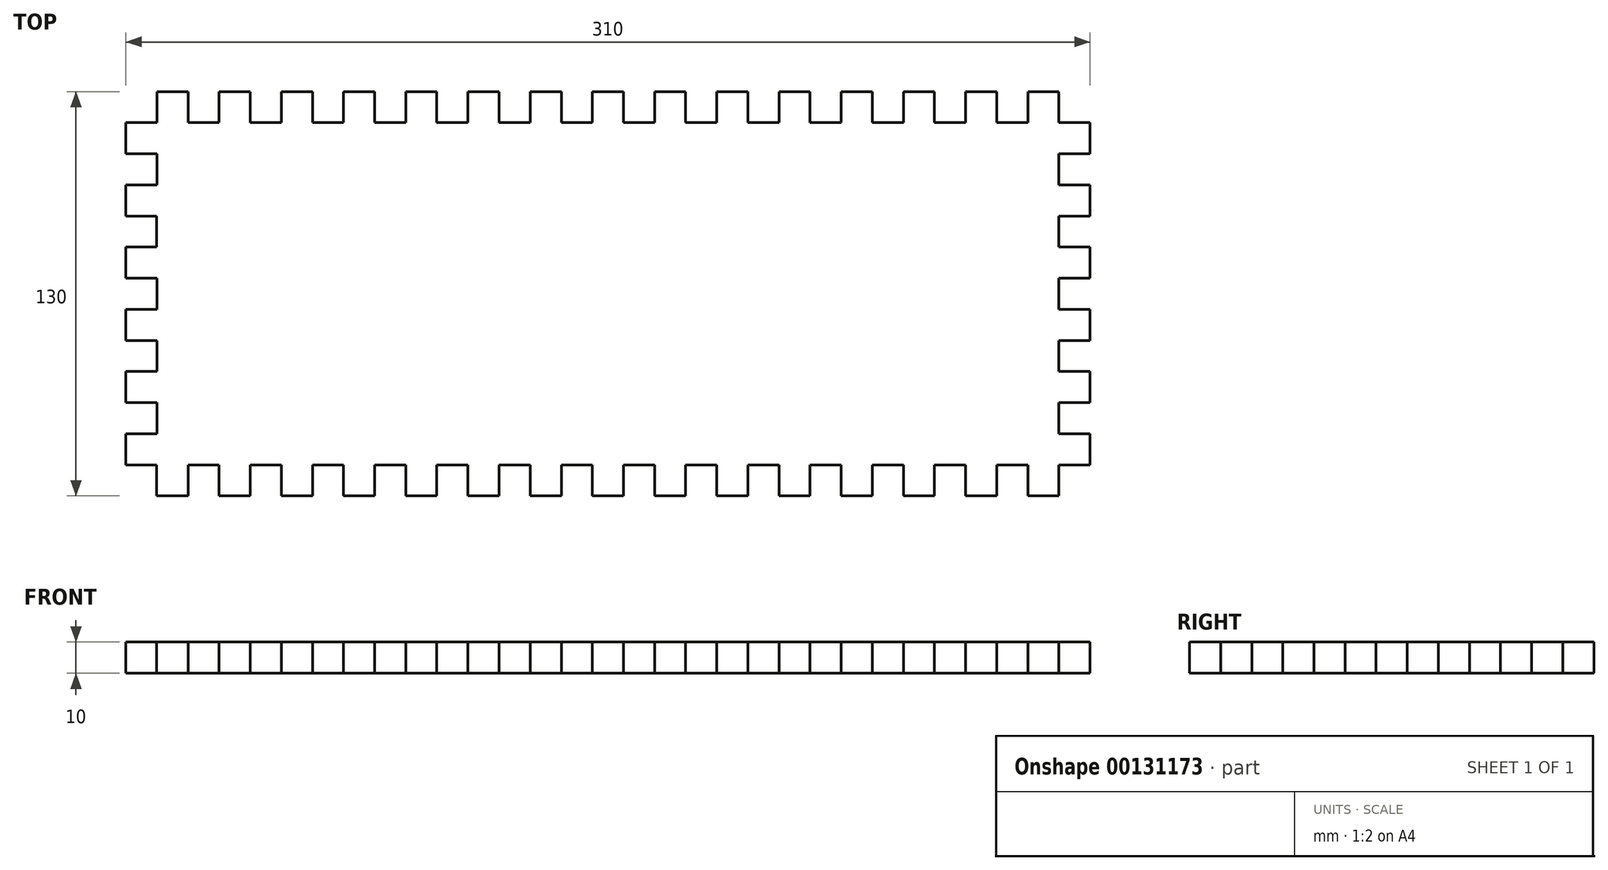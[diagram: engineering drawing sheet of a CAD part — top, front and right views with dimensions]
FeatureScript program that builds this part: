
annotation { "Feature Type Name" : "Feature", "Feature Type Description" : "" }
export const myFeature = defineFeature(function(context is Context, id is Id, definition is map)
    precondition{}
    {
        {
            var Q0;
            Q0=qCreatedBy(makeId("Top.planeOp"),FACE);
            var sketch = newSketch(context, id + "F0", { "sketchPlane" : qUnion([Q0])});
            skLineSegment(sketch, "E0.bottom", {"start": v(-145.09, -65) * mm, "end": v(-135, -65) * mm});
            skLineSegment(sketch, "E0.left", {"start": v(-155, -55) * mm, "end": v(-155, -45) * mm});
            skLineSegment(sketch, "E0.right", {"start": v(155, -55) * mm, "end": v(155, -45) * mm});
            skPoint(sketch, "E0.middle", {"position": v(0, 0) * mm});
            skLineSegment(sketch, "E1.top", {"start": v(-155, 55) * mm, "end": v(-145, 55) * mm});
            skLineSegment(sketch, "E1.right", {"start": v(-145, 65) * mm, "end": v(-145, 55) * mm});
            skLineSegment(sketch, "E2.top", {"start": v(-155, 45) * mm, "end": v(-145, 45) * mm});
            skLineSegment(sketch, "E2.left", {"start": v(-155, 55) * mm, "end": v(-155, 45) * mm});
            skLineSegment(sketch, "E2.right", {"start": v(-145, 55) * mm, "end": v(-145, 45) * mm});
            skLineSegment(sketch, "E3.top", {"start": v(-155, 35) * mm, "end": v(-145, 35) * mm});
            skLineSegment(sketch, "E3.right", {"start": v(-145, 45) * mm, "end": v(-145, 35) * mm});
            skLineSegment(sketch, "E4.top", {"start": v(-155, 25) * mm, "end": v(-145, 25) * mm});
            skLineSegment(sketch, "E4.left", {"start": v(-155, 35) * mm, "end": v(-155, 25) * mm});
            skLineSegment(sketch, "E4.right", {"start": v(-145, 35) * mm, "end": v(-145, 25) * mm});
            skLineSegment(sketch, "E5.bottom", {"start": v(-155, 25) * mm, "end": v(-145.13, 25) * mm});
            skLineSegment(sketch, "E5.top", {"start": v(-155, 15) * mm, "end": v(-145.13, 15) * mm});
            skLineSegment(sketch, "E5.right", {"start": v(-145.13, 25) * mm, "end": v(-145.13, 15) * mm});
            skLineSegment(sketch, "E6.bottom", {"start": v(-155, 15) * mm, "end": v(-145, 15) * mm});
            skLineSegment(sketch, "E6.top", {"start": v(-155, 5) * mm, "end": v(-145, 5) * mm});
            skLineSegment(sketch, "E6.left", {"start": v(-155, 15) * mm, "end": v(-155, 5) * mm});
            skLineSegment(sketch, "E6.right", {"start": v(-145, 15) * mm, "end": v(-145, 5) * mm});
            skPoint(sketch, "E7.orphan", {"position": v(-155, 65) * mm});
            skLineSegment(sketch, "E8.trimOffspring", {"start": v(-155, 45) * mm, "end": v(-155, 55) * mm});
            skLineSegment(sketch, "E9.trimOffspring", {"start": v(-155, 25) * mm, "end": v(-155, 35) * mm});
            skPoint(sketch, "E10.orphan", {"position": v(155, 65) * mm});
            skLineSegment(sketch, "E11.top", {"start": v(-155, -5) * mm, "end": v(-145, -5) * mm});
            skLineSegment(sketch, "E11.right", {"start": v(-145, 5) * mm, "end": v(-145, -5) * mm});
            skLineSegment(sketch, "E12.top", {"start": v(-155, -15) * mm, "end": v(-145, -15) * mm});
            skLineSegment(sketch, "E12.left", {"start": v(-155, -5) * mm, "end": v(-155, -15) * mm});
            skLineSegment(sketch, "E12.right", {"start": v(-145, -5) * mm, "end": v(-145, -15) * mm});
            skLineSegment(sketch, "E13.top", {"start": v(-155, -25) * mm, "end": v(-145, -25) * mm});
            skLineSegment(sketch, "E13.right", {"start": v(-145, -15) * mm, "end": v(-145, -25) * mm});
            skLineSegment(sketch, "E14.top", {"start": v(-155, -35) * mm, "end": v(-145, -35) * mm});
            skLineSegment(sketch, "E14.left", {"start": v(-155, -25) * mm, "end": v(-155, -35) * mm});
            skLineSegment(sketch, "E14.right", {"start": v(-145, -25) * mm, "end": v(-145, -35) * mm});
            skLineSegment(sketch, "E15.top", {"start": v(-155, -45) * mm, "end": v(-145, -45) * mm});
            skLineSegment(sketch, "E15.right", {"start": v(-145, -35) * mm, "end": v(-145, -45) * mm});
            skLineSegment(sketch, "E16.top", {"start": v(-155, -55) * mm, "end": v(-145, -55) * mm});
            skLineSegment(sketch, "E16.left", {"start": v(-155, -45) * mm, "end": v(-155, -55) * mm});
            skLineSegment(sketch, "E16.right", {"start": v(-145, -45) * mm, "end": v(-145, -55) * mm});
            skLineSegment(sketch, "E17.bottom", {"start": v(-155, -55) * mm, "end": v(-145.09, -55) * mm});
            skLineSegment(sketch, "E17.right", {"start": v(-145.09, -55) * mm, "end": v(-145.09, -65) * mm});
            skLineSegment(sketch, "E18.trimOffspring", {"start": v(-155, 5) * mm, "end": v(-155, 15) * mm});
            skLineSegment(sketch, "E19.trimOffspring", {"start": v(-155, -15) * mm, "end": v(-155, -5) * mm});
            skLineSegment(sketch, "E20.trimOffspring", {"start": v(-155, -35) * mm, "end": v(-155, -25) * mm});
            skPoint(sketch, "E21.orphan", {"position": v(-155, -65) * mm});
            skLineSegment(sketch, "E22.bottom", {"start": v(-145, 65) * mm, "end": v(-135, 65) * mm});
            skLineSegment(sketch, "E22.top", {"start": v(-145, 55) * mm, "end": v(-135, 55) * mm});
            skLineSegment(sketch, "E22.right", {"start": v(-135, 65) * mm, "end": v(-135, 55) * mm});
            skLineSegment(sketch, "E23.top", {"start": v(-135, 55) * mm, "end": v(-125, 55) * mm});
            skLineSegment(sketch, "E23.right", {"start": v(-125, 65) * mm, "end": v(-125, 55) * mm});
            skLineSegment(sketch, "E24.bottom", {"start": v(-125, 65) * mm, "end": v(-115, 65) * mm});
            skLineSegment(sketch, "E24.top", {"start": v(-125, 55) * mm, "end": v(-115, 55) * mm});
            skLineSegment(sketch, "E24.right", {"start": v(-115, 65) * mm, "end": v(-115, 55) * mm});
            skLineSegment(sketch, "E25.top", {"start": v(-115, 55) * mm, "end": v(-105, 55) * mm});
            skLineSegment(sketch, "E25.right", {"start": v(-105, 65) * mm, "end": v(-105, 55) * mm});
            skLineSegment(sketch, "E26.bottom", {"start": v(-105, 65) * mm, "end": v(-95, 65) * mm});
            skLineSegment(sketch, "E26.top", {"start": v(-105, 55) * mm, "end": v(-95, 55) * mm});
            skLineSegment(sketch, "E26.right", {"start": v(-95, 65) * mm, "end": v(-95, 55) * mm});
            skLineSegment(sketch, "E27.top", {"start": v(-95, 55) * mm, "end": v(-85, 55) * mm});
            skLineSegment(sketch, "E27.right", {"start": v(-85, 65) * mm, "end": v(-85, 55) * mm});
            skLineSegment(sketch, "E28.bottom", {"start": v(-85, 65) * mm, "end": v(-75, 65) * mm});
            skLineSegment(sketch, "E28.top", {"start": v(-85, 55) * mm, "end": v(-75, 55) * mm});
            skLineSegment(sketch, "E28.right", {"start": v(-75, 65) * mm, "end": v(-75, 55) * mm});
            skLineSegment(sketch, "E29.top", {"start": v(-75, 55) * mm, "end": v(-65, 55) * mm});
            skLineSegment(sketch, "E29.right", {"start": v(-65, 65) * mm, "end": v(-65, 55) * mm});
            skLineSegment(sketch, "E30.bottom", {"start": v(-65, 65) * mm, "end": v(-55, 65) * mm});
            skLineSegment(sketch, "E30.top", {"start": v(-65, 55) * mm, "end": v(-55, 55) * mm});
            skLineSegment(sketch, "E30.right", {"start": v(-55, 65) * mm, "end": v(-55, 55) * mm});
            skLineSegment(sketch, "E31.top", {"start": v(-55, 55) * mm, "end": v(-45, 55) * mm});
            skLineSegment(sketch, "E31.right", {"start": v(-45, 65) * mm, "end": v(-45, 55) * mm});
            skLineSegment(sketch, "E32.bottom", {"start": v(-45, 65) * mm, "end": v(-35, 65) * mm});
            skLineSegment(sketch, "E32.top", {"start": v(-45, 55) * mm, "end": v(-35, 55) * mm});
            skLineSegment(sketch, "E32.right", {"start": v(-35, 65) * mm, "end": v(-35, 55) * mm});
            skLineSegment(sketch, "E33.top", {"start": v(-35, 55) * mm, "end": v(-25, 55) * mm});
            skLineSegment(sketch, "E33.right", {"start": v(-25, 65) * mm, "end": v(-25, 55) * mm});
            skLineSegment(sketch, "E34.bottom", {"start": v(-25, 65) * mm, "end": v(-15, 65) * mm});
            skLineSegment(sketch, "E34.top", {"start": v(-25, 55) * mm, "end": v(-15, 55) * mm});
            skLineSegment(sketch, "E34.right", {"start": v(-15, 65) * mm, "end": v(-15, 55) * mm});
            skLineSegment(sketch, "E35.top", {"start": v(-15, 55) * mm, "end": v(-5, 55) * mm});
            skLineSegment(sketch, "E35.right", {"start": v(-5, 65) * mm, "end": v(-5, 55) * mm});
            skLineSegment(sketch, "E36.bottom", {"start": v(-5, 65) * mm, "end": v(5, 65) * mm});
            skLineSegment(sketch, "E36.top", {"start": v(-5, 54.5) * mm, "end": v(5, 54.5) * mm});
            skLineSegment(sketch, "E36.left", {"start": v(-5, 65) * mm, "end": v(-5, 54.5) * mm});
            skLineSegment(sketch, "E36.right", {"start": v(5, 65) * mm, "end": v(5, 54.5) * mm});
            skLineSegment(sketch, "E37.top", {"start": v(5, 55) * mm, "end": v(15, 55) * mm});
            skLineSegment(sketch, "E37.left", {"start": v(5, 65) * mm, "end": v(5, 55) * mm});
            skLineSegment(sketch, "E37.right", {"start": v(15, 65) * mm, "end": v(15, 55) * mm});
            skLineSegment(sketch, "E38.bottom", {"start": v(15, 65) * mm, "end": v(25, 65) * mm});
            skLineSegment(sketch, "E38.top", {"start": v(15, 55) * mm, "end": v(25, 55) * mm});
            skLineSegment(sketch, "E38.right", {"start": v(25, 65) * mm, "end": v(25, 55) * mm});
            skLineSegment(sketch, "E39.top", {"start": v(25, 55) * mm, "end": v(35, 55) * mm});
            skLineSegment(sketch, "E39.right", {"start": v(35, 65) * mm, "end": v(35, 55) * mm});
            skLineSegment(sketch, "E40.bottom", {"start": v(35, 65) * mm, "end": v(45, 65) * mm});
            skLineSegment(sketch, "E40.top", {"start": v(35, 55) * mm, "end": v(45, 55) * mm});
            skLineSegment(sketch, "E40.right", {"start": v(45, 65) * mm, "end": v(45, 55) * mm});
            skLineSegment(sketch, "E41.top", {"start": v(45, 55) * mm, "end": v(55, 55) * mm});
            skLineSegment(sketch, "E41.right", {"start": v(55, 65) * mm, "end": v(55, 55) * mm});
            skLineSegment(sketch, "E42.bottom", {"start": v(55, 65) * mm, "end": v(65, 65) * mm});
            skLineSegment(sketch, "E42.top", {"start": v(55, 55) * mm, "end": v(65, 55) * mm});
            skLineSegment(sketch, "E42.right", {"start": v(65, 65) * mm, "end": v(65, 55) * mm});
            skLineSegment(sketch, "E43.top", {"start": v(65, 55) * mm, "end": v(75, 55) * mm});
            skLineSegment(sketch, "E43.right", {"start": v(75, 65) * mm, "end": v(75, 55) * mm});
            skLineSegment(sketch, "E44.bottom", {"start": v(75, 65) * mm, "end": v(85, 65) * mm});
            skLineSegment(sketch, "E44.top", {"start": v(75, 55) * mm, "end": v(85, 55) * mm});
            skLineSegment(sketch, "E44.right", {"start": v(85, 65) * mm, "end": v(85, 55) * mm});
            skLineSegment(sketch, "E45.top", {"start": v(85, 55) * mm, "end": v(95, 55) * mm});
            skLineSegment(sketch, "E45.right", {"start": v(95, 65) * mm, "end": v(95, 55) * mm});
            skLineSegment(sketch, "E46.bottom", {"start": v(95, 65) * mm, "end": v(105, 65) * mm});
            skLineSegment(sketch, "E46.top", {"start": v(95, 55) * mm, "end": v(105, 55) * mm});
            skLineSegment(sketch, "E46.right", {"start": v(105, 65) * mm, "end": v(105, 55) * mm});
            skLineSegment(sketch, "E47.top", {"start": v(105, 55) * mm, "end": v(115, 55) * mm});
            skLineSegment(sketch, "E47.right", {"start": v(115, 65) * mm, "end": v(115, 55) * mm});
            skLineSegment(sketch, "E48.bottom", {"start": v(115, 65) * mm, "end": v(125, 65) * mm});
            skLineSegment(sketch, "E48.top", {"start": v(115, 55) * mm, "end": v(125, 55) * mm});
            skLineSegment(sketch, "E48.right", {"start": v(125, 65) * mm, "end": v(125, 55) * mm});
            skLineSegment(sketch, "E49.top", {"start": v(125, 55) * mm, "end": v(135, 55) * mm});
            skLineSegment(sketch, "E49.right", {"start": v(135, 65) * mm, "end": v(135, 55) * mm});
            skLineSegment(sketch, "E50.bottom", {"start": v(135, 65) * mm, "end": v(145, 65) * mm});
            skLineSegment(sketch, "E50.top", {"start": v(135, 55) * mm, "end": v(145, 55) * mm});
            skLineSegment(sketch, "E50.right", {"start": v(145, 65) * mm, "end": v(145, 55) * mm});
            skLineSegment(sketch, "E51.top", {"start": v(145, 55) * mm, "end": v(155, 55) * mm});
            skLineSegment(sketch, "E52.bottom", {"start": v(-145, -55) * mm, "end": v(-135, -55) * mm});
            skLineSegment(sketch, "E52.top", {"start": v(-145, -65) * mm, "end": v(-135, -65) * mm});
            skLineSegment(sketch, "E52.left", {"start": v(-145, -55) * mm, "end": v(-145, -65) * mm});
            skLineSegment(sketch, "E52.right", {"start": v(-135, -55) * mm, "end": v(-135, -65) * mm});
            skLineSegment(sketch, "E53.bottom", {"start": v(-135, -55) * mm, "end": v(-125, -55) * mm});
            skLineSegment(sketch, "E53.right", {"start": v(-125, -55) * mm, "end": v(-125, -65) * mm});
            skLineSegment(sketch, "E54.bottom", {"start": v(-125, -55) * mm, "end": v(-115, -55) * mm});
            skLineSegment(sketch, "E54.top", {"start": v(-125, -65) * mm, "end": v(-115, -65) * mm});
            skLineSegment(sketch, "E54.right", {"start": v(-115, -55) * mm, "end": v(-115, -65) * mm});
            skLineSegment(sketch, "E55.bottom", {"start": v(-115, -55) * mm, "end": v(-105, -55) * mm});
            skLineSegment(sketch, "E55.right", {"start": v(-105, -55) * mm, "end": v(-105, -65) * mm});
            skLineSegment(sketch, "E56.bottom", {"start": v(-105, -55) * mm, "end": v(-95, -55) * mm});
            skLineSegment(sketch, "E56.top", {"start": v(-105, -65) * mm, "end": v(-95, -65) * mm});
            skLineSegment(sketch, "E56.right", {"start": v(-95, -55) * mm, "end": v(-95, -65) * mm});
            skLineSegment(sketch, "E57.bottom", {"start": v(-95, -55) * mm, "end": v(-85, -55) * mm});
            skLineSegment(sketch, "E57.right", {"start": v(-85, -55) * mm, "end": v(-85, -65) * mm});
            skLineSegment(sketch, "E58.bottom", {"start": v(-85, -55) * mm, "end": v(-75, -55) * mm});
            skLineSegment(sketch, "E58.top", {"start": v(-85, -65) * mm, "end": v(-75, -65) * mm});
            skLineSegment(sketch, "E58.right", {"start": v(-75, -55) * mm, "end": v(-75, -65) * mm});
            skLineSegment(sketch, "E59.bottom", {"start": v(-75, -55) * mm, "end": v(-65, -55) * mm});
            skLineSegment(sketch, "E59.right", {"start": v(-65, -55) * mm, "end": v(-65, -65) * mm});
            skLineSegment(sketch, "E60.bottom", {"start": v(-65, -55) * mm, "end": v(-55, -55) * mm});
            skLineSegment(sketch, "E60.top", {"start": v(-65, -65) * mm, "end": v(-55, -65) * mm});
            skLineSegment(sketch, "E60.right", {"start": v(-55, -55) * mm, "end": v(-55, -65) * mm});
            skLineSegment(sketch, "E61.bottom", {"start": v(-55, -55) * mm, "end": v(-45, -55) * mm});
            skLineSegment(sketch, "E61.right", {"start": v(-45, -55) * mm, "end": v(-45, -65) * mm});
            skLineSegment(sketch, "E62.bottom", {"start": v(-45, -55) * mm, "end": v(-35, -55) * mm});
            skLineSegment(sketch, "E62.top", {"start": v(-45, -65) * mm, "end": v(-35, -65) * mm});
            skLineSegment(sketch, "E62.right", {"start": v(-35, -55) * mm, "end": v(-35, -65) * mm});
            skLineSegment(sketch, "E63.bottom", {"start": v(-35, -55) * mm, "end": v(-25, -55) * mm});
            skLineSegment(sketch, "E63.right", {"start": v(-25, -55) * mm, "end": v(-25, -65) * mm});
            skLineSegment(sketch, "E64.bottom", {"start": v(-25, -55) * mm, "end": v(-15, -55) * mm});
            skLineSegment(sketch, "E64.top", {"start": v(-25, -65) * mm, "end": v(-15, -65) * mm});
            skLineSegment(sketch, "E64.right", {"start": v(-15, -55) * mm, "end": v(-15, -65) * mm});
            skLineSegment(sketch, "E65.bottom", {"start": v(-15, -55) * mm, "end": v(-5, -55) * mm});
            skLineSegment(sketch, "E65.right", {"start": v(-5, -55) * mm, "end": v(-5, -65) * mm});
            skLineSegment(sketch, "E66.bottom", {"start": v(-5, -55) * mm, "end": v(5, -55) * mm});
            skLineSegment(sketch, "E66.top", {"start": v(-5, -65) * mm, "end": v(5, -65) * mm});
            skLineSegment(sketch, "E66.right", {"start": v(5, -55) * mm, "end": v(5, -65) * mm});
            skLineSegment(sketch, "E67.bottom", {"start": v(5, -55) * mm, "end": v(15, -55) * mm});
            skLineSegment(sketch, "E67.right", {"start": v(15, -55) * mm, "end": v(15, -65) * mm});
            skLineSegment(sketch, "E68.bottom", {"start": v(15, -55) * mm, "end": v(25, -55) * mm});
            skLineSegment(sketch, "E68.top", {"start": v(15, -65) * mm, "end": v(25, -65) * mm});
            skLineSegment(sketch, "E68.right", {"start": v(25, -55) * mm, "end": v(25, -65) * mm});
            skLineSegment(sketch, "E69.bottom", {"start": v(25, -55) * mm, "end": v(35, -55) * mm});
            skLineSegment(sketch, "E69.right", {"start": v(35, -55) * mm, "end": v(35, -65) * mm});
            skLineSegment(sketch, "E70.bottom", {"start": v(35, -55) * mm, "end": v(45, -55) * mm});
            skLineSegment(sketch, "E70.top", {"start": v(35, -65) * mm, "end": v(45, -65) * mm});
            skLineSegment(sketch, "E70.right", {"start": v(45, -55) * mm, "end": v(45, -65) * mm});
            skLineSegment(sketch, "E71.bottom", {"start": v(45, -55) * mm, "end": v(55, -55) * mm});
            skLineSegment(sketch, "E71.right", {"start": v(55, -55) * mm, "end": v(55, -65) * mm});
            skLineSegment(sketch, "E72.bottom", {"start": v(55, -55) * mm, "end": v(65, -55) * mm});
            skLineSegment(sketch, "E72.top", {"start": v(55, -65) * mm, "end": v(65, -65) * mm});
            skLineSegment(sketch, "E72.right", {"start": v(65, -55) * mm, "end": v(65, -65) * mm});
            skLineSegment(sketch, "E73.bottom", {"start": v(65, -55) * mm, "end": v(75, -55) * mm});
            skLineSegment(sketch, "E73.right", {"start": v(75, -55) * mm, "end": v(75, -65) * mm});
            skLineSegment(sketch, "E74.bottom", {"start": v(75, -55) * mm, "end": v(85, -55) * mm});
            skLineSegment(sketch, "E74.top", {"start": v(75, -65) * mm, "end": v(85, -65) * mm});
            skLineSegment(sketch, "E74.right", {"start": v(85, -55) * mm, "end": v(85, -65) * mm});
            skLineSegment(sketch, "E75.bottom", {"start": v(85, -55) * mm, "end": v(95, -55) * mm});
            skLineSegment(sketch, "E75.right", {"start": v(95, -55) * mm, "end": v(95, -65) * mm});
            skLineSegment(sketch, "E76.bottom", {"start": v(95, -55) * mm, "end": v(105, -55) * mm});
            skLineSegment(sketch, "E76.top", {"start": v(95, -65) * mm, "end": v(105, -65) * mm});
            skLineSegment(sketch, "E76.right", {"start": v(105, -55) * mm, "end": v(105, -65) * mm});
            skLineSegment(sketch, "E77.bottom", {"start": v(105, -55) * mm, "end": v(115, -55) * mm});
            skLineSegment(sketch, "E77.right", {"start": v(115, -55) * mm, "end": v(115, -65) * mm});
            skLineSegment(sketch, "E78.bottom", {"start": v(115, -55) * mm, "end": v(125, -55) * mm});
            skLineSegment(sketch, "E78.top", {"start": v(115, -65) * mm, "end": v(125, -65) * mm});
            skLineSegment(sketch, "E78.right", {"start": v(125, -55) * mm, "end": v(125, -65) * mm});
            skLineSegment(sketch, "E79.bottom", {"start": v(125, -55) * mm, "end": v(135, -55) * mm});
            skLineSegment(sketch, "E79.right", {"start": v(135, -55) * mm, "end": v(135, -65) * mm});
            skLineSegment(sketch, "E80.bottom", {"start": v(135, -55) * mm, "end": v(145, -55) * mm});
            skLineSegment(sketch, "E80.top", {"start": v(135, -65) * mm, "end": v(145, -65) * mm});
            skLineSegment(sketch, "E80.right", {"start": v(145, -55) * mm, "end": v(145, -65) * mm});
            skLineSegment(sketch, "E81.bottom", {"start": v(145, -55) * mm, "end": v(155, -55) * mm});
            skPoint(sketch, "E81.right.end.orphan", {"position": v(155, -65) * mm});
            skLineSegment(sketch, "E82.top", {"start": v(145, 45) * mm, "end": v(155, 45) * mm});
            skLineSegment(sketch, "E82.left", {"start": v(145, 55) * mm, "end": v(145, 45) * mm});
            skLineSegment(sketch, "E82.right", {"start": v(155, 55) * mm, "end": v(155, 45) * mm});
            skLineSegment(sketch, "E83.top", {"start": v(145, 35) * mm, "end": v(155, 35) * mm});
            skLineSegment(sketch, "E83.left", {"start": v(145, 45) * mm, "end": v(145, 35) * mm});
            skLineSegment(sketch, "E84.top", {"start": v(145, 25) * mm, "end": v(155, 25) * mm});
            skLineSegment(sketch, "E84.left", {"start": v(145, 35) * mm, "end": v(145, 25) * mm});
            skLineSegment(sketch, "E84.right", {"start": v(155, 35) * mm, "end": v(155, 25) * mm});
            skLineSegment(sketch, "E85.top", {"start": v(145, 15) * mm, "end": v(155, 15) * mm});
            skLineSegment(sketch, "E85.left", {"start": v(145, 25) * mm, "end": v(145, 15) * mm});
            skLineSegment(sketch, "E86.top", {"start": v(145, 5) * mm, "end": v(155, 5) * mm});
            skLineSegment(sketch, "E86.left", {"start": v(145, 15) * mm, "end": v(145, 5) * mm});
            skLineSegment(sketch, "E86.right", {"start": v(155, 15) * mm, "end": v(155, 5) * mm});
            skLineSegment(sketch, "E87.top", {"start": v(145, -5) * mm, "end": v(155, -5) * mm});
            skLineSegment(sketch, "E87.left", {"start": v(145, 5) * mm, "end": v(145, -5) * mm});
            skLineSegment(sketch, "E88.top", {"start": v(145, -15) * mm, "end": v(155, -15) * mm});
            skLineSegment(sketch, "E88.left", {"start": v(145, -5) * mm, "end": v(145, -15) * mm});
            skLineSegment(sketch, "E88.right", {"start": v(155, -5) * mm, "end": v(155, -15) * mm});
            skLineSegment(sketch, "E89.top", {"start": v(145, -25) * mm, "end": v(155, -25) * mm});
            skLineSegment(sketch, "E89.left", {"start": v(145, -15) * mm, "end": v(145, -25) * mm});
            skLineSegment(sketch, "E90.top", {"start": v(145, -35) * mm, "end": v(155, -35) * mm});
            skLineSegment(sketch, "E90.left", {"start": v(145, -25) * mm, "end": v(145, -35) * mm});
            skLineSegment(sketch, "E90.right", {"start": v(155, -25) * mm, "end": v(155, -35) * mm});
            skLineSegment(sketch, "E91.top", {"start": v(145, -45) * mm, "end": v(155, -45) * mm});
            skLineSegment(sketch, "E91.left", {"start": v(145, -35) * mm, "end": v(145, -45) * mm});
            skLineSegment(sketch, "E92", {"start": v(145, -45) * mm, "end": v(145, -55) * mm});
            skLineSegment(sketch, "E93.trimOffspring", {"start": v(155, 45) * mm, "end": v(155, 55) * mm});
            skLineSegment(sketch, "E94.trimOffspring", {"start": v(155, 25) * mm, "end": v(155, 35) * mm});
            skLineSegment(sketch, "E95.trimOffspring", {"start": v(155, 5) * mm, "end": v(155, 15) * mm});
            skLineSegment(sketch, "E96.trimOffspring", {"start": v(155, -15) * mm, "end": v(155, -5) * mm});
            skLineSegment(sketch, "E97.trimOffspring", {"start": v(155, -35) * mm, "end": v(155, -25) * mm});
            skSolve(sketch);
        }
        {
            var Q0;
            Q0=makeQuery(id+"F0.imprint","IMPRINT",FACE,{"disambiguationData":[TD([[makeQuery(id+"F0.imprint","IMPRINT",EDGE,{"derivedFrom":sQuery(id+"F0.wireOp",EDGE,"E0.bottom")}),1.0]])]});
            var Q1;
            Q1=makeQuery(id+"F0.imprint","IMPRINT",FACE,{"disambiguationData":[TD([[makeQuery(id+"F0.imprint","IMPRINT",EDGE,{"derivedFrom":sQuery(id+"F0.wireOp",EDGE,"E1.top")}),-1.0]])]});
            var Q2;
            Q2=makeQuery(id+"F0.imprint","IMPRINT",FACE,{"disambiguationData":[TD([[makeQuery(id+"F0.imprint","IMPRINT",EDGE,{"derivedFrom":sQuery(id+"F0.wireOp",EDGE,"E3.top")}),-1.0]])]});
            var Q3;
            {var subQ2=sQuery(id+"F0.wireOp",EDGE,"E6.right");Q3=makeQuery(id+"F0.imprint","IMPRINT",FACE,{"disambiguationData":[TD([[makeQuery(id+"F0.imprint","IMPRINT",EDGE,{"derivedFrom":subQ2}),-1.0]])]});}
            var Q4;
            Q4=makeQuery(id+"F0.imprint","IMPRINT",FACE,{"disambiguationData":[TD([[makeQuery(id+"F0.imprint","IMPRINT",EDGE,{"derivedFrom":sQuery(id+"F0.wireOp",EDGE,"E11.top")}),-1.0]])]});
            var Q5;
            Q5=makeQuery(id+"F0.imprint","IMPRINT",FACE,{"disambiguationData":[TD([[makeQuery(id+"F0.imprint","IMPRINT",EDGE,{"derivedFrom":sQuery(id+"F0.wireOp",EDGE,"E13.top")}),-1.0]])]});
            var Q6;
            Q6=makeQuery(id+"F0.imprint","IMPRINT",FACE,{"disambiguationData":[TD([[makeQuery(id+"F0.imprint","IMPRINT",EDGE,{"derivedFrom":sQuery(id+"F0.wireOp",EDGE,"E15.top")}),-1.0]])]});
            var Q7;
            Q7=makeQuery(id+"F0.imprint","IMPRINT",FACE,{"disambiguationData":[TD([[makeQuery(id+"F0.imprint","IMPRINT",EDGE,{"derivedFrom":sQuery(id+"F0.wireOp",EDGE,"E52.bottom")}),-1.0]])]});
            var Q8;
            Q8=makeQuery(id+"F0.imprint","IMPRINT",FACE,{"disambiguationData":[TD([[makeQuery(id+"F0.imprint","IMPRINT",EDGE,{"derivedFrom":sQuery(id+"F0.wireOp",EDGE,"E0.right")}),1.0]])]});
            var Q9;
            Q9=makeQuery(id+"F0.imprint","IMPRINT",FACE,{"disambiguationData":[TD([[makeQuery(id+"F0.imprint","IMPRINT",EDGE,{"derivedFrom":sQuery(id+"F0.wireOp",EDGE,"E22.bottom")}),-1.0]])]});
            var Q10;
            Q10=makeQuery(id+"F0.imprint","IMPRINT",FACE,{"disambiguationData":[TD([[makeQuery(id+"F0.imprint","IMPRINT",EDGE,{"derivedFrom":sQuery(id+"F0.wireOp",EDGE,"E24.top")}),1.0]])]});
            var Q11;
            Q11=makeQuery(id+"F0.imprint","IMPRINT",FACE,{"disambiguationData":[TD([[makeQuery(id+"F0.imprint","IMPRINT",EDGE,{"derivedFrom":sQuery(id+"F0.wireOp",EDGE,"E26.bottom")}),-1.0]])]});
            var Q12;
            Q12=makeQuery(id+"F0.imprint","IMPRINT",FACE,{"disambiguationData":[TD([[makeQuery(id+"F0.imprint","IMPRINT",EDGE,{"derivedFrom":sQuery(id+"F0.wireOp",EDGE,"E28.top")}),1.0]])]});
            var Q13;
            Q13=makeQuery(id+"F0.imprint","IMPRINT",FACE,{"disambiguationData":[TD([[makeQuery(id+"F0.imprint","IMPRINT",EDGE,{"derivedFrom":sQuery(id+"F0.wireOp",EDGE,"E30.top")}),1.0]])]});
            var Q14;
            Q14=makeQuery(id+"F0.imprint","IMPRINT",FACE,{"disambiguationData":[TD([[makeQuery(id+"F0.imprint","IMPRINT",EDGE,{"derivedFrom":sQuery(id+"F0.wireOp",EDGE,"E32.top")}),1.0]])]});
            var Q15;
            Q15=makeQuery(id+"F0.imprint","IMPRINT",FACE,{"disambiguationData":[TD([[makeQuery(id+"F0.imprint","IMPRINT",EDGE,{"derivedFrom":sQuery(id+"F0.wireOp",EDGE,"E34.top")}),1.0]])]});
            var Q16;
            {var subQ2=sQuery(id+"F0.wireOp",EDGE,"E36.top");Q16=makeQuery(id+"F0.imprint","IMPRINT",FACE,{"disambiguationData":[TD([[makeQuery(id+"F0.imprint","IMPRINT",EDGE,{"derivedFrom":subQ2}),1.0]])]});}
            var Q17;
            Q17=makeQuery(id+"F0.imprint","IMPRINT",FACE,{"disambiguationData":[TD([[makeQuery(id+"F0.imprint","IMPRINT",EDGE,{"derivedFrom":sQuery(id+"F0.wireOp",EDGE,"E38.top")}),1.0]])]});
            var Q18;
            Q18=makeQuery(id+"F0.imprint","IMPRINT",FACE,{"disambiguationData":[TD([[makeQuery(id+"F0.imprint","IMPRINT",EDGE,{"derivedFrom":sQuery(id+"F0.wireOp",EDGE,"E40.top")}),1.0]])]});
            var Q19;
            Q19=makeQuery(id+"F0.imprint","IMPRINT",FACE,{"disambiguationData":[TD([[makeQuery(id+"F0.imprint","IMPRINT",EDGE,{"derivedFrom":sQuery(id+"F0.wireOp",EDGE,"E42.top")}),1.0]])]});
            var Q20;
            Q20=makeQuery(id+"F0.imprint","IMPRINT",FACE,{"disambiguationData":[TD([[makeQuery(id+"F0.imprint","IMPRINT",EDGE,{"derivedFrom":sQuery(id+"F0.wireOp",EDGE,"E44.top")}),1.0]])]});
            var Q21;
            {var subQ2=sQuery(id+"F0.wireOp",EDGE,"E46.top");Q21=makeQuery(id+"F0.imprint","IMPRINT",FACE,{"disambiguationData":[TD([[makeQuery(id+"F0.imprint","IMPRINT",EDGE,{"derivedFrom":subQ2}),1.0]])]});}
            var Q22;
            Q22=makeQuery(id+"F0.imprint","IMPRINT",FACE,{"disambiguationData":[TD([[makeQuery(id+"F0.imprint","IMPRINT",EDGE,{"derivedFrom":sQuery(id+"F0.wireOp",EDGE,"E48.top")}),1.0]])]});
            var Q23;
            Q23=makeQuery(id+"F0.imprint","IMPRINT",FACE,{"disambiguationData":[TD([[makeQuery(id+"F0.imprint","IMPRINT",EDGE,{"derivedFrom":sQuery(id+"F0.wireOp",EDGE,"E50.top")}),1.0]])]});
            var Q24;
            Q24=makeQuery(id+"F0.imprint","IMPRINT",FACE,{"disambiguationData":[TD([[makeQuery(id+"F0.imprint","IMPRINT",EDGE,{"derivedFrom":sQuery(id+"F0.wireOp",EDGE,"E54.bottom")}),-1.0]])]});
            var Q25;
            Q25=makeQuery(id+"F0.imprint","IMPRINT",FACE,{"disambiguationData":[TD([[makeQuery(id+"F0.imprint","IMPRINT",EDGE,{"derivedFrom":sQuery(id+"F0.wireOp",EDGE,"E56.bottom")}),-1.0]])]});
            var Q26;
            Q26=makeQuery(id+"F0.imprint","IMPRINT",FACE,{"disambiguationData":[TD([[makeQuery(id+"F0.imprint","IMPRINT",EDGE,{"derivedFrom":sQuery(id+"F0.wireOp",EDGE,"E58.bottom")}),-1.0]])]});
            var Q27;
            Q27=makeQuery(id+"F0.imprint","IMPRINT",FACE,{"disambiguationData":[TD([[makeQuery(id+"F0.imprint","IMPRINT",EDGE,{"derivedFrom":sQuery(id+"F0.wireOp",EDGE,"E60.bottom")}),-1.0]])]});
            var Q28;
            Q28=makeQuery(id+"F0.imprint","IMPRINT",FACE,{"disambiguationData":[TD([[makeQuery(id+"F0.imprint","IMPRINT",EDGE,{"derivedFrom":sQuery(id+"F0.wireOp",EDGE,"E62.bottom")}),-1.0]])]});
            var Q29;
            Q29=makeQuery(id+"F0.imprint","IMPRINT",FACE,{"disambiguationData":[TD([[makeQuery(id+"F0.imprint","IMPRINT",EDGE,{"derivedFrom":sQuery(id+"F0.wireOp",EDGE,"E64.bottom")}),-1.0]])]});
            var Q30;
            Q30=makeQuery(id+"F0.imprint","IMPRINT",FACE,{"disambiguationData":[TD([[makeQuery(id+"F0.imprint","IMPRINT",EDGE,{"derivedFrom":sQuery(id+"F0.wireOp",EDGE,"E66.bottom")}),-1.0]])]});
            var Q31;
            Q31=makeQuery(id+"F0.imprint","IMPRINT",FACE,{"disambiguationData":[TD([[makeQuery(id+"F0.imprint","IMPRINT",EDGE,{"derivedFrom":sQuery(id+"F0.wireOp",EDGE,"E68.bottom")}),-1.0]])]});
            var Q32;
            Q32=makeQuery(id+"F0.imprint","IMPRINT",FACE,{"disambiguationData":[TD([[makeQuery(id+"F0.imprint","IMPRINT",EDGE,{"derivedFrom":sQuery(id+"F0.wireOp",EDGE,"E70.bottom")}),-1.0]])]});
            var Q33;
            Q33=makeQuery(id+"F0.imprint","IMPRINT",FACE,{"disambiguationData":[TD([[makeQuery(id+"F0.imprint","IMPRINT",EDGE,{"derivedFrom":sQuery(id+"F0.wireOp",EDGE,"E72.bottom")}),-1.0]])]});
            var Q34;
            Q34=makeQuery(id+"F0.imprint","IMPRINT",FACE,{"disambiguationData":[TD([[makeQuery(id+"F0.imprint","IMPRINT",EDGE,{"derivedFrom":sQuery(id+"F0.wireOp",EDGE,"E74.bottom")}),-1.0]])]});
            var Q35;
            Q35=makeQuery(id+"F0.imprint","IMPRINT",FACE,{"disambiguationData":[TD([[makeQuery(id+"F0.imprint","IMPRINT",EDGE,{"derivedFrom":sQuery(id+"F0.wireOp",EDGE,"E76.bottom")}),-1.0]])]});
            var Q36;
            Q36=makeQuery(id+"F0.imprint","IMPRINT",FACE,{"disambiguationData":[TD([[makeQuery(id+"F0.imprint","IMPRINT",EDGE,{"derivedFrom":sQuery(id+"F0.wireOp",EDGE,"E78.bottom")}),-1.0]])]});
            var Q37;
            Q37=makeQuery(id+"F0.imprint","IMPRINT",FACE,{"disambiguationData":[TD([[makeQuery(id+"F0.imprint","IMPRINT",EDGE,{"derivedFrom":sQuery(id+"F0.wireOp",EDGE,"E80.bottom")}),-1.0]])]});
            var Q38;
            Q38=makeQuery(id+"F0.imprint","IMPRINT",FACE,{"disambiguationData":[TD([[makeQuery(id+"F0.imprint","IMPRINT",EDGE,{"derivedFrom":sQuery(id+"F0.wireOp",EDGE,"E51.top")}),-1.0]])]});
            var Q39;
            Q39=makeQuery(id+"F0.imprint","IMPRINT",FACE,{"disambiguationData":[TD([[makeQuery(id+"F0.imprint","IMPRINT",EDGE,{"derivedFrom":sQuery(id+"F0.wireOp",EDGE,"E83.top")}),-1.0]])]});
            var Q40;
            Q40=makeQuery(id+"F0.imprint","IMPRINT",FACE,{"disambiguationData":[TD([[makeQuery(id+"F0.imprint","IMPRINT",EDGE,{"derivedFrom":sQuery(id+"F0.wireOp",EDGE,"E85.top")}),-1.0]])]});
            var Q41;
            Q41=makeQuery(id+"F0.imprint","IMPRINT",FACE,{"disambiguationData":[TD([[makeQuery(id+"F0.imprint","IMPRINT",EDGE,{"derivedFrom":sQuery(id+"F0.wireOp",EDGE,"E87.top")}),-1.0]])]});
            var Q42;
            Q42=makeQuery(id+"F0.imprint","IMPRINT",FACE,{"disambiguationData":[TD([[makeQuery(id+"F0.imprint","IMPRINT",EDGE,{"derivedFrom":sQuery(id+"F0.wireOp",EDGE,"E89.top")}),-1.0]])]});
            var Q43;
            Q43=makeQuery(id+"F0.imprint","IMPRINT",FACE,{"disambiguationData":[TD([[makeQuery(id+"F0.imprint","IMPRINT",EDGE,{"derivedFrom":sQuery(id+"F0.wireOp",EDGE,"E2.right")}),1.0]])]});
            var Q44;
            Q44 = qSketchRegion(id + "F0", true);
            extrude(context, id + "F1", {"entities" : qUnion([Q0, Q1, Q2, Q3, Q4, Q5, Q6, Q7, Q8, Q9, Q10, Q11, Q12, Q13, Q14, Q15, Q16, Q17, Q18, Q19, Q20, Q21, Q22, Q23, Q24, Q25, Q26, Q27, Q28, Q29, Q30, Q31, Q32, Q33, Q34, Q35, Q36, Q37, Q38, Q39, Q40, Q41, Q42, Q43, Q44]), "depth" : 10 * mm});
        }
    });
